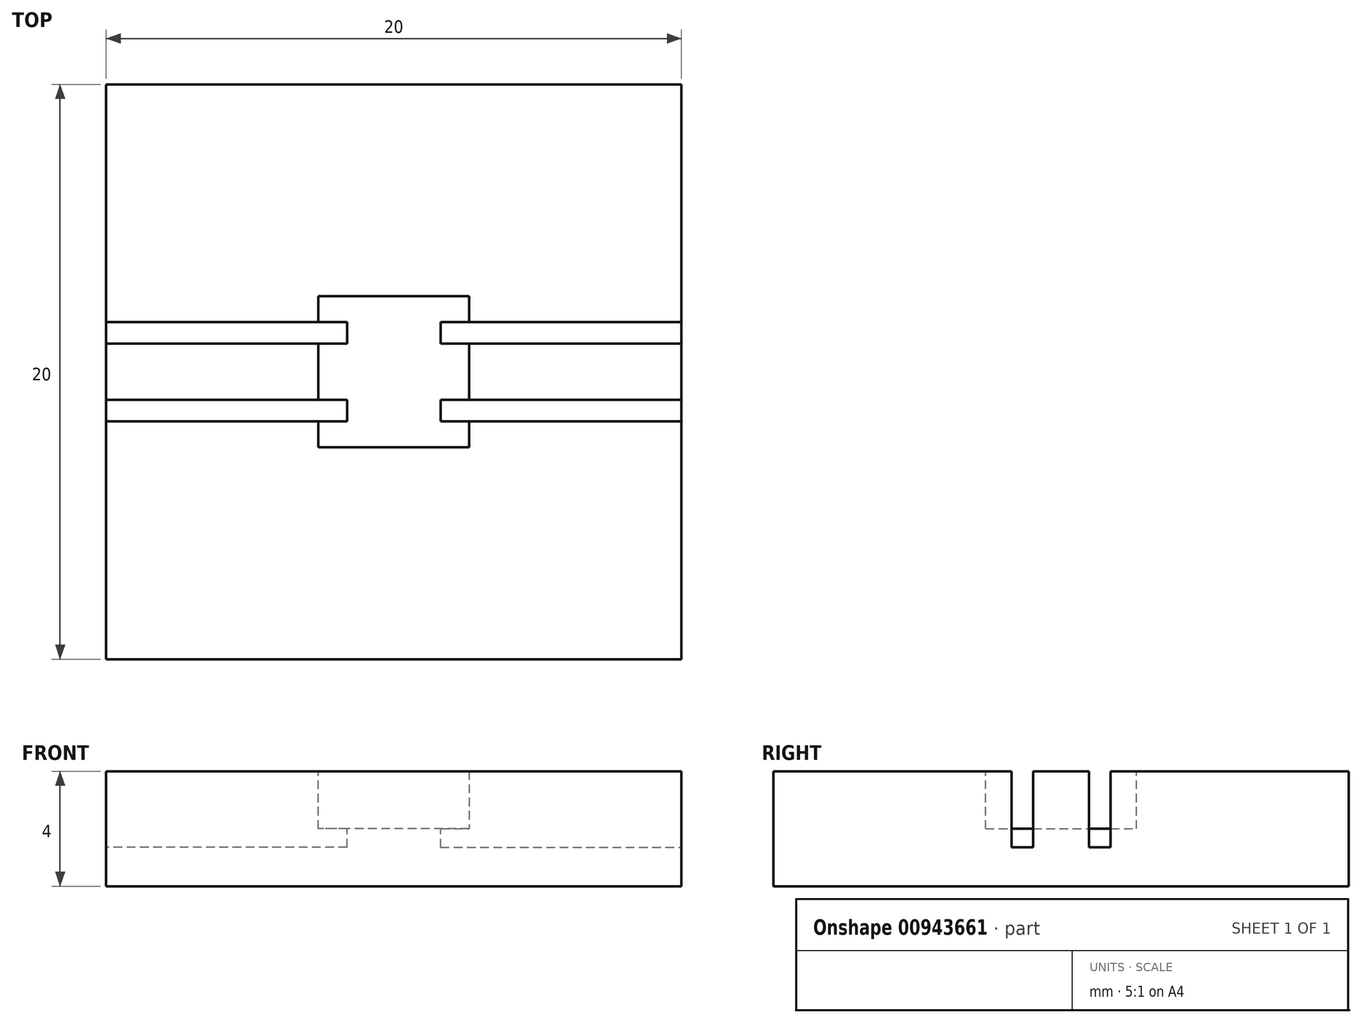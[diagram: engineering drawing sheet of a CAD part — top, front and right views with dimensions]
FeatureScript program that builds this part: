
annotation { "Feature Type Name" : "Feature", "Feature Type Description" : "" }
export const myFeature = defineFeature(function(context is Context, id is Id, definition is map)
    precondition{}
    {
        {
            var Q0;
            Q0=qCreatedBy(makeId("Top.planeOp"),FACE);
            var sketch = newSketch(context, id + "F0", { "sketchPlane" : qUnion([Q0])});
            skLineSegment(sketch, "E0.bottom", {"start": v(-10, 10) * mm, "end": v(10, 10) * mm});
            skLineSegment(sketch, "E0.top", {"start": v(-10, -10) * mm, "end": v(10, -10) * mm});
            skLineSegment(sketch, "E0.left", {"start": v(-10, 10) * mm, "end": v(-10, -10) * mm});
            skLineSegment(sketch, "E0.right", {"start": v(10, 10) * mm, "end": v(10, -10) * mm});
            skPoint(sketch, "E0.middle", {"position": v(0, 0) * mm});
            skSolve(sketch);
        }
        {
            var Q0;
            Q0 = qSketchRegion(id + "F0", true);
            extrude(context, id + "F1", {"entities" : qUnion([Q0]), "depth" : 4 * mm, "offsetDistance" : 25 * mm});
        }
        {
            var Q0;
            Q0=makeQuery(id+"F1.opExtrude","CAP_FACE",FACE,{"disambiguationData":[OSD([sQuery(id+"F0.wireOp",EDGE,"E0.bottom"),sQuery(id+"F0.wireOp",EDGE,"E0.top"),sQuery(id+"F0.wireOp",EDGE,"E0.left"),sQuery(id+"F0.wireOp",EDGE,"E0.right")])],"isStart":false});
            var sketch = newSketch(context, id + "F2", { "sketchPlane" : qUnion([Q0])});
            skLineSegment(sketch, "E1.bottom", {"start": v(2.62, -2.62) * mm, "end": v(-2.62, -2.63) * mm});
            skLineSegment(sketch, "E1.top", {"start": v(2.62, 2.63) * mm, "end": v(-2.62, 2.62) * mm});
            skLineSegment(sketch, "E1.left", {"start": v(2.62, -2.62) * mm, "end": v(2.62, 2.63) * mm});
            skLineSegment(sketch, "E1.right", {"start": v(-2.62, -2.63) * mm, "end": v(-2.62, 2.62) * mm});
            skPoint(sketch, "E1.middle", {"position": v(0, 0) * mm});
            skSolve(sketch);
        }
        {
            var Q0;
            Q0 = qSketchRegion(id + "F2", true);
            extrude(context, id + "F3", {"entities" : qUnion([Q0]), "operationType" : NewBodyOperationType.REMOVE, "oppositeDirection" : true, "depth" : 2 * mm, "offsetDistance" : 25 * mm});
        }
        {
            var Q0;
            Q0=makeQuery(id+"F1.opExtrude","CAP_FACE",FACE,{"disambiguationData":[OSD([sQuery(id+"F0.wireOp",EDGE,"E0.bottom"),sQuery(id+"F0.wireOp",EDGE,"E0.top"),sQuery(id+"F0.wireOp",EDGE,"E0.left"),sQuery(id+"F0.wireOp",EDGE,"E0.right")])],"isStart":false});
            var sketch = newSketch(context, id + "F4", { "sketchPlane" : qUnion([Q0])});
            skLineSegment(sketch, "E2.bottom", {"start": v(-1.63, 1.72) * mm, "end": v(-10, 1.72) * mm});
            skLineSegment(sketch, "E2.top", {"start": v(-1.62, 0.97) * mm, "end": v(-10, 0.97) * mm});
            skLineSegment(sketch, "E2.left", {"start": v(-1.63, 1.72) * mm, "end": v(-1.62, 0.97) * mm});
            skLineSegment(sketch, "E2.right", {"start": v(-10, 1.72) * mm, "end": v(-10, 0.97) * mm});
            skLineSegment(sketch, "E3.bottom", {"start": v(1.63, 1.73) * mm, "end": v(10, 1.73) * mm});
            skLineSegment(sketch, "E3.top", {"start": v(1.63, 0.98) * mm, "end": v(10, 0.98) * mm});
            skLineSegment(sketch, "E3.left", {"start": v(1.63, 1.73) * mm, "end": v(1.63, 0.98) * mm});
            skLineSegment(sketch, "E3.right", {"start": v(10, 1.73) * mm, "end": v(10, 0.98) * mm});
            skLineSegment(sketch, "E4.bottom", {"start": v(1.63, -0.98) * mm, "end": v(10, -0.97) * mm});
            skLineSegment(sketch, "E4.top", {"start": v(1.63, -1.72) * mm, "end": v(10, -1.72) * mm});
            skLineSegment(sketch, "E4.left", {"start": v(1.63, -0.97) * mm, "end": v(1.63, -1.72) * mm});
            skLineSegment(sketch, "E4.right", {"start": v(10, -0.97) * mm, "end": v(10, -1.72) * mm});
            skLineSegment(sketch, "E5.bottom", {"start": v(-1.63, -0.98) * mm, "end": v(-10, -0.98) * mm});
            skLineSegment(sketch, "E5.top", {"start": v(-1.63, -1.73) * mm, "end": v(-10, -1.73) * mm});
            skLineSegment(sketch, "E5.left", {"start": v(-1.63, -0.98) * mm, "end": v(-1.63, -1.73) * mm});
            skLineSegment(sketch, "E5.right", {"start": v(-10, -0.98) * mm, "end": v(-10, -1.73) * mm});
            skSolve(sketch);
        }
        {
            var Q0;
            Q0 = qSketchRegion(id + "F4", true);
            extrude(context, id + "F5", {"entities" : qUnion([Q0]), "operationType" : NewBodyOperationType.REMOVE, "oppositeDirection" : true, "depth" : 2.65 * mm, "offsetDistance" : 25 * mm});
        }
    });
